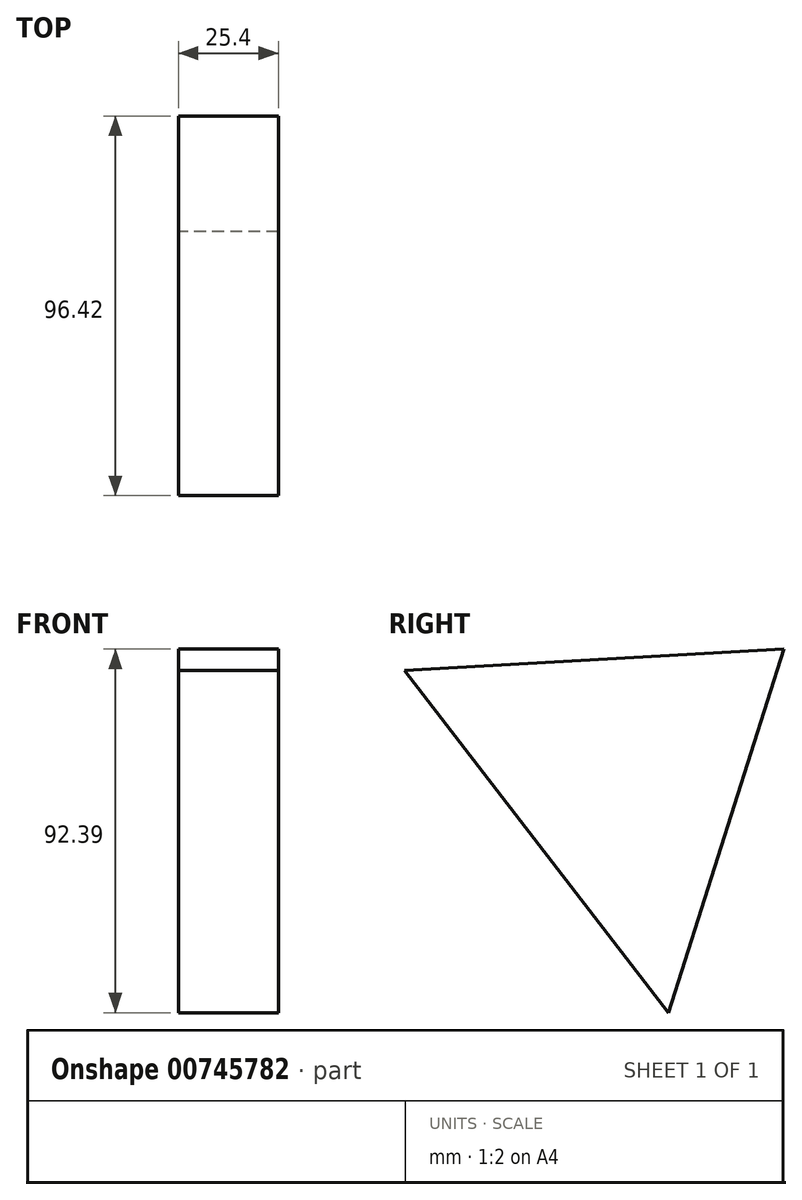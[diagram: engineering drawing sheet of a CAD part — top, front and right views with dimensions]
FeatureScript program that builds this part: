
annotation { "Feature Type Name" : "Feature", "Feature Type Description" : "" }
export const myFeature = defineFeature(function(context is Context, id is Id, definition is map)
    precondition{}
    {
        {
            var Q0;
            Q0=qCreatedBy(makeId("Right.planeOp"),FACE);
            var sketch = newSketch(context, id + "F0", { "sketchPlane" : qUnion([Q0])});
            skLineSegment(sketch, "E0", {"start": v(-45.33, 41.59) * mm, "end": v(21.73, -45.33) * mm});
            skLineSegment(sketch, "E1", {"start": v(21.73, -45.33) * mm, "end": v(51.09, 47.06) * mm});
            skLineSegment(sketch, "E2", {"start": v(51.09, 47.06) * mm, "end": v(-45.33, 41.59) * mm});
            skSolve(sketch);
        }
        {
            var Q0;
            Q0 = qSketchRegion(id + "F0", true);
            extrude(context, id + "F1", {"entities" : qUnion([Q0]), "depth" : 25.4 * mm, "offsetDistance" : 25.4 * mm});
        }
    });
